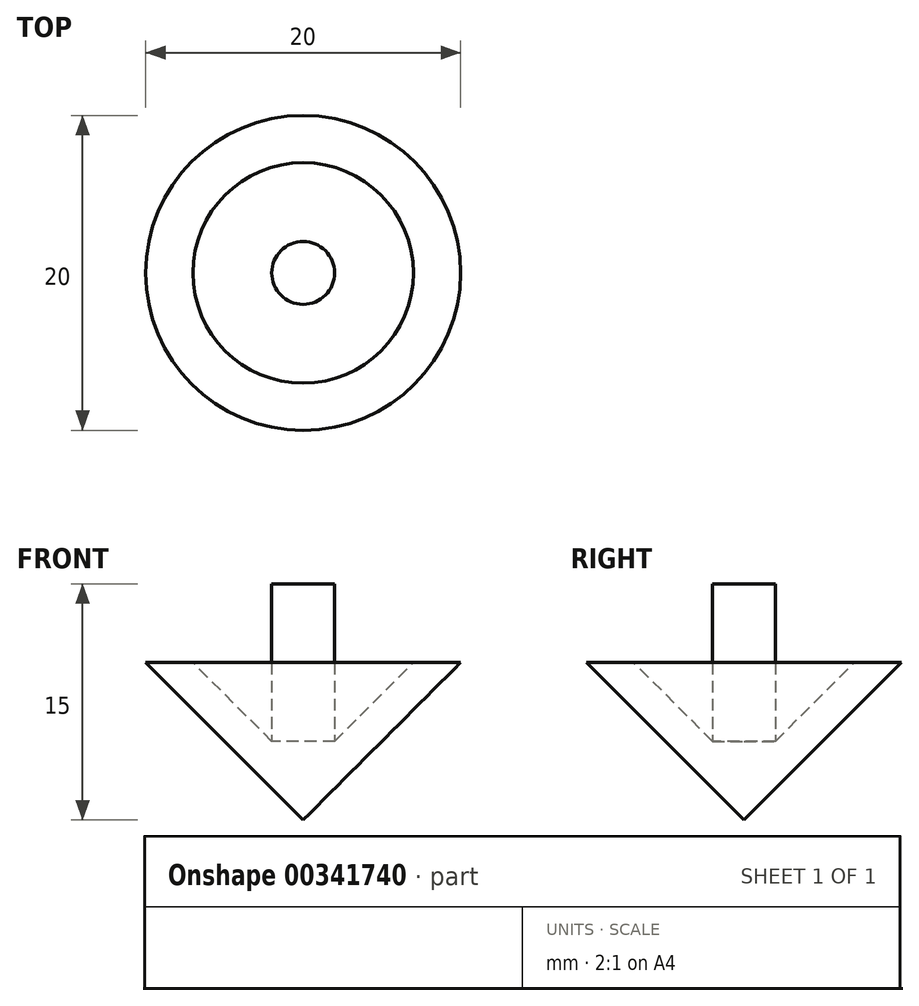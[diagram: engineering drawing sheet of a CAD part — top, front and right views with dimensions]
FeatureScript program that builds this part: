
annotation { "Feature Type Name" : "Feature", "Feature Type Description" : "" }
export const myFeature = defineFeature(function(context is Context, id is Id, definition is map)
    precondition{}
    {
        {
            var Q0;
            Q0=qCreatedBy(makeId("Front.planeOp"),FACE);
            var sketch = newSketch(context, id + "F0", { "sketchPlane" : qUnion([Q0])});
            skLineSegment(sketch, "E0", {"start": v(0, 0) * mm, "end": v(10, 10) * mm});
            skLineSegment(sketch, "E1", {"start": v(10, 10) * mm, "end": v(0, 10) * mm});
            skLineSegment(sketch, "E2", {"start": v(0, 10) * mm, "end": v(0, 0) * mm});
            skSolve(sketch);
        }
        {
            var Q0;
            Q0 = qSketchRegion(id + "F0", true);
            var Q1;
            Q1=sQuery(id+"F0.wireOp",EDGE,"E2");
            revolve(context, id + "F1", {"entities" : qUnion([Q0]), "axis" : qUnion([Q1]), "revolveType" : RevolveType.FULL});
        }
        {
            var Q0;
            Q0=qCreatedBy(makeId("Front.planeOp"),FACE);
            var sketch = newSketch(context, id + "F2", { "sketchPlane" : qUnion([Q0])});
            skLineSegment(sketch, "E3", {"start": v(0, 10) * mm, "end": v(0, 3) * mm});
            skLineSegment(sketch, "E4", {"start": v(0, 3) * mm, "end": v(7, 10) * mm});
            skLineSegment(sketch, "E5", {"start": v(7, 10) * mm, "end": v(0, 10) * mm});
            skLineSegment(sketch, "E6.0", {"start": v(-10, 10) * mm, "end": v(10, 10) * mm, "construction": true});
            skSolve(sketch);
        }
        {
            var Q0;
            Q0 = qSketchRegion(id + "F2", true);
            var Q1;
            Q1=sQuery(id+"F2.wireOp",EDGE,"E3");
            revolve(context, id + "F3", {"operationType" : NewBodyOperationType.REMOVE, "entities" : qUnion([Q0]), "axis" : qUnion([Q1]), "revolveType" : RevolveType.FULL, "oppositeDirection" : true});
        }
        {
            var Q0;
            Q0=makeQuery(id+"F1.opRevolve","SWEPT_FACE",FACE,{"disambiguationData":[OSD([sQuery(id+"F0.wireOp",EDGE,"E1")])]});
            var sketch = newSketch(context, id + "F4", { "sketchPlane" : qUnion([Q0])});
            skCircle(sketch, "E7", {"center": v(0, 0) * mm, "radius": 2 * mm});
            skSolve(sketch);
        }
        {
            var Q0;
            Q0 = qSketchRegion(id + "F4", true);
            extrude(context, id + "F5", {"entities" : qUnion([Q0]), "operationType" : NewBodyOperationType.ADD, "depth" : 5 * mm, "hasSecondDirection" : true, "secondDirectionOppositeDirection" : true, "secondDirectionDepth" : 8 * mm});
        }
    });
